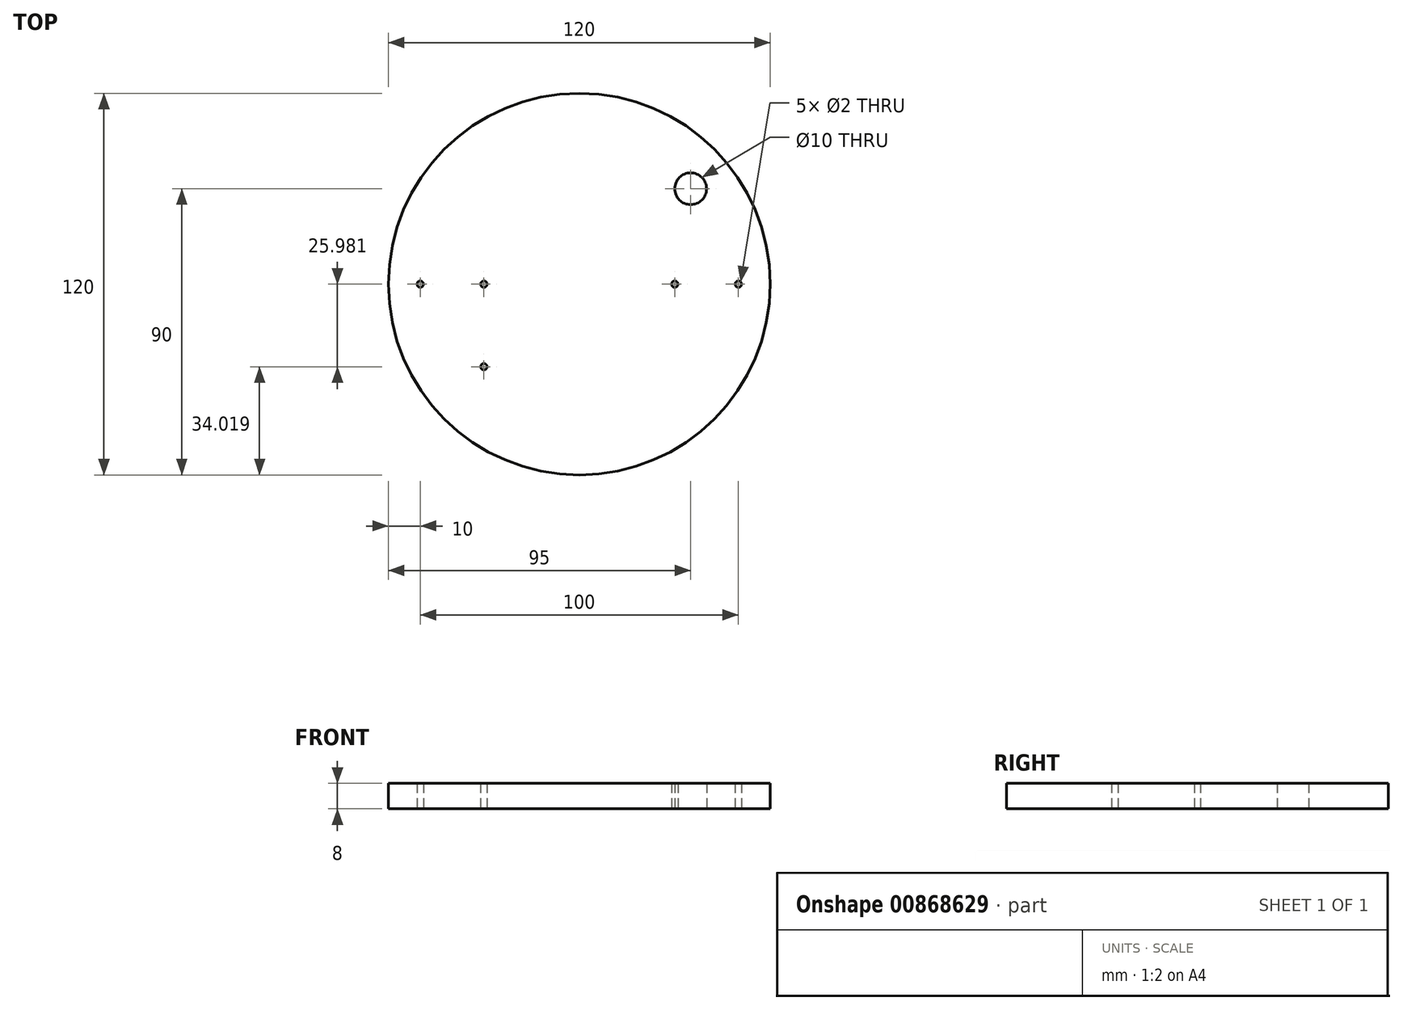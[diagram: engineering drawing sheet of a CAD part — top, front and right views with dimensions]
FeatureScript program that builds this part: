
annotation { "Feature Type Name" : "Feature", "Feature Type Description" : "" }
export const myFeature = defineFeature(function(context is Context, id is Id, definition is map)
    precondition{}
    {
        {
            var Q0;
            Q0=qCreatedBy(makeId("Top.planeOp"),FACE);
            var sketch = newSketch(context, id + "F0", { "sketchPlane" : qUnion([Q0])});
            skCircle(sketch, "E0", {"center": v(0, 0) * mm, "radius": 60 * mm});
            skCircle(sketch, "E1", {"center": v(-50, 0) * mm, "radius": 1 * mm});
            skCircle(sketch, "E2", {"center": v(-30, 0) * mm, "radius": 1 * mm});
            skCircle(sketch, "E3", {"center": v(50, 0) * mm, "radius": 1 * mm});
            skCircle(sketch, "E4", {"center": v(30, 0) * mm, "radius": 1 * mm});
            skCircle(sketch, "E5", {"center": v(35, 30) * mm, "radius": 5 * mm});
            skPoint(sketch, "E6", {"position": v(35, 0) * mm});
            skLineSegment(sketch, "E7", {"start": v(35, 0) * mm, "end": v(35, 48.73) * mm});
            skCircle(sketch, "E8", {"center": v(-30, -25.98) * mm, "radius": 1 * mm});
            skLineSegment(sketch, "E9", {"start": v(-30, 0) * mm, "end": v(-30, -51.96) * mm});
            skSolve(sketch);
        }
        {
            var Q0;
            Q0=makeQuery(id+"F0.imprint","IMPRINT",FACE,{"disambiguationData":[TD([[makeQuery(id+"F0.imprint","IMPRINT",EDGE,{"derivedFrom":sQuery(id+"F0.wireOp",EDGE,"E0")}),1.0]])]});
            extrude(context, id + "F1", {"entities" : qUnion([Q0]), "depth" : 8 * mm, "offsetDistance" : 25 * mm});
        }
    });
